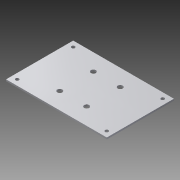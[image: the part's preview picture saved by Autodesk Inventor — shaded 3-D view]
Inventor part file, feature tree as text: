
AUTODESK INVENTOR PART (.ipt)
format: ipt  version: 2015 (Build 190159000, 159)  size: 116,224 bytes
history: native  units: mm
features: sketch x3, hole x2, extrude x1
ambient origin geometry x8: Origin, YZ Plane, XZ Plane, XY Plane, X Axis, Y Axis, Z Axis, Center Point
bodies: Body1 (feature_tree)
feature tree (6):
  extrude  "押し出し5"  Depth=90.0mm
  hole  "穴5"  [1 undecoded]
  hole  "穴6"  [1 undecoded]
  sketch  "スケッチ12"
  sketch  "スケッチ13"
  sketch  "スケッチ14"
note: 2 required parameter values undecoded (feature->parameter linkage not recoverable at this tier; creation-order binding heuristic only, values carry confidence <= 0.55)
